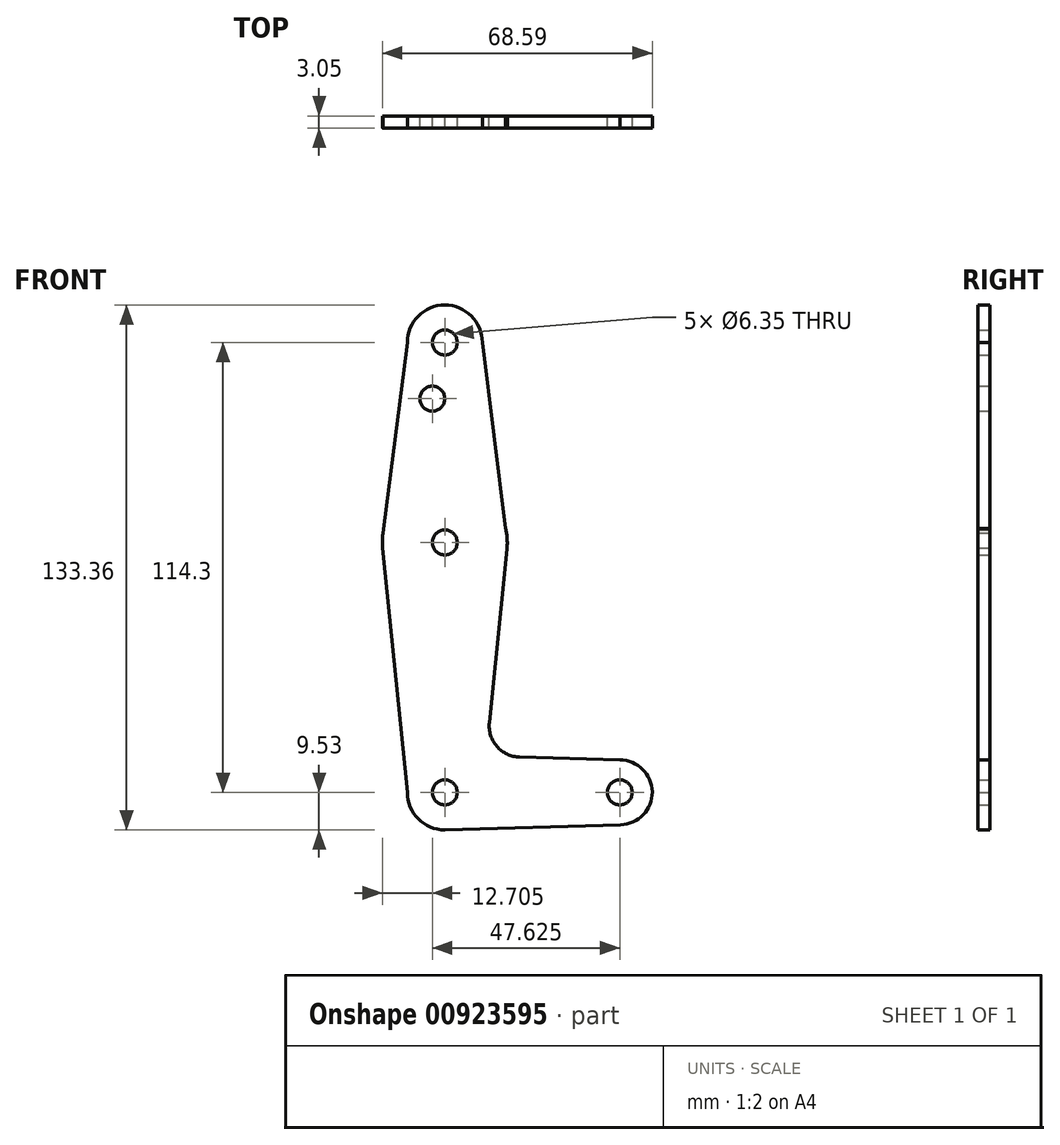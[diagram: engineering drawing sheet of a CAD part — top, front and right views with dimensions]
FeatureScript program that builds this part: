
annotation { "Feature Type Name" : "Feature", "Feature Type Description" : "" }
export const myFeature = defineFeature(function(context is Context, id is Id, definition is map)
    precondition{}
    {
        {
            var Q0;
            Q0=qCreatedBy(makeId("Front.planeOp"),FACE);
            var sketch = newSketch(context, id + "F0", { "sketchPlane" : qUnion([Q0])});
            skCircle(sketch, "E0", {"center": v(0, 114.3) * mm, "radius": 9.53 * mm});
            skCircle(sketch, "E1", {"center": v(0, 63.5) * mm, "radius": 15.88 * mm});
            skCircle(sketch, "E2", {"center": v(0, 0) * mm, "radius": 9.53 * mm});
            skCircle(sketch, "E3", {"center": v(44.45, 0) * mm, "radius": 8.26 * mm});
            skLineSegment(sketch, "E4", {"start": v(0, 114.3) * mm, "end": v(0, 0) * mm, "construction": true});
            skLineSegment(sketch, "E5", {"start": v(0, 0) * mm, "end": v(44.45, 0) * mm, "construction": true});
            skLineSegment(sketch, "E6", {"start": v(9.52, 114.3) * mm, "end": v(15.47, 67.05) * mm});
            skLineSegment(sketch, "E7", {"start": v(-9.53, 114.3) * mm, "end": v(-15.7, 65.85) * mm});
            skLineSegment(sketch, "E8", {"start": v(-9.53, 0) * mm, "end": v(-15.81, 62.1) * mm});
            skLineSegment(sketch, "E9", {"start": v(11.32, 17.73) * mm, "end": v(15.8, 61.9) * mm});
            skLineSegment(sketch, "E10", {"start": v(0, -9.53) * mm, "end": v(44.69, -8.25) * mm});
            skLineSegment(sketch, "E11", {"start": v(44.45, 8.26) * mm, "end": v(19, 8.98) * mm});
            skCircle(sketch, "E12", {"center": v(0, 114.3) * mm, "radius": 3.18 * mm});
            skCircle(sketch, "E13", {"center": v(-3.17, 100.03) * mm, "radius": 3.18 * mm});
            skCircle(sketch, "E14", {"center": v(0, 63.5) * mm, "radius": 3.18 * mm});
            skCircle(sketch, "E15", {"center": v(0, 0) * mm, "radius": 3.18 * mm});
            skCircle(sketch, "E16", {"center": v(44.45, 0) * mm, "radius": 3.18 * mm});
            skPoint(sketch, "E17.newPointB", {"position": v(0, 9.53) * mm});
            skArc(sketch, "E17.filletArc", {"start": v(11.32, 17.73) * mm, "mid": v(13.26, 11.69) * mm, "end": v(19, 8.98) * mm});
            skSolve(sketch);
        }
        {
            var Q0;
            {var subQ1=sQuery(id+"F0.wireOp",EDGE,"E6");Q0=makeQuery(id+"F0.imprint","IMPRINT",FACE,{"disambiguationData":[TD([[makeQuery(id+"F0.imprint","IMPRINT",EDGE,{"derivedFrom":subQ1}),-1.0]])]});}
            var Q1;
            {var subQ10=sQuery(id+"F0.wireOp",EDGE,"E9");Q1=makeQuery(id+"F0.imprint","IMPRINT",FACE,{"disambiguationData":[TD([[makeQuery(id+"F0.imprint","IMPRINT",EDGE,{"derivedFrom":subQ10}),1.0]])]});}
            var Q2;
            Q2=makeQuery(id+"F0.imprint","IMPRINT",FACE,{"disambiguationData":[TD([[makeQuery(id+"F0.imprint","IMPRINT",EDGE,{"derivedFrom":sQuery(id+"F0.wireOp",EDGE,"E14")}),-1.0]])]});
            var Q3;
            Q3=makeQuery(id+"F0.imprint","IMPRINT",FACE,{"disambiguationData":[TD([[makeQuery(id+"F0.imprint","IMPRINT",EDGE,{"derivedFrom":sQuery(id+"F0.wireOp",EDGE,"E12")}),-1.0]])]});
            var Q4;
            Q4=makeQuery(id+"F0.imprint","IMPRINT",FACE,{"disambiguationData":[TD([[makeQuery(id+"F0.imprint","IMPRINT",EDGE,{"derivedFrom":sQuery(id+"F0.wireOp",EDGE,"E15")}),-1.0]])]});
            var Q5;
            Q5=makeQuery(id+"F0.imprint","IMPRINT",FACE,{"disambiguationData":[TD([[makeQuery(id+"F0.imprint","IMPRINT",EDGE,{"derivedFrom":sQuery(id+"F0.wireOp",EDGE,"E16")}),-1.0]])]});
            extrude(context, id + "F1", {"entities" : qUnion([Q0, Q1, Q2, Q3, Q4, Q5]), "depth" : 3.05 * mm, "offsetDistance" : 25.4 * mm});
        }
    });
